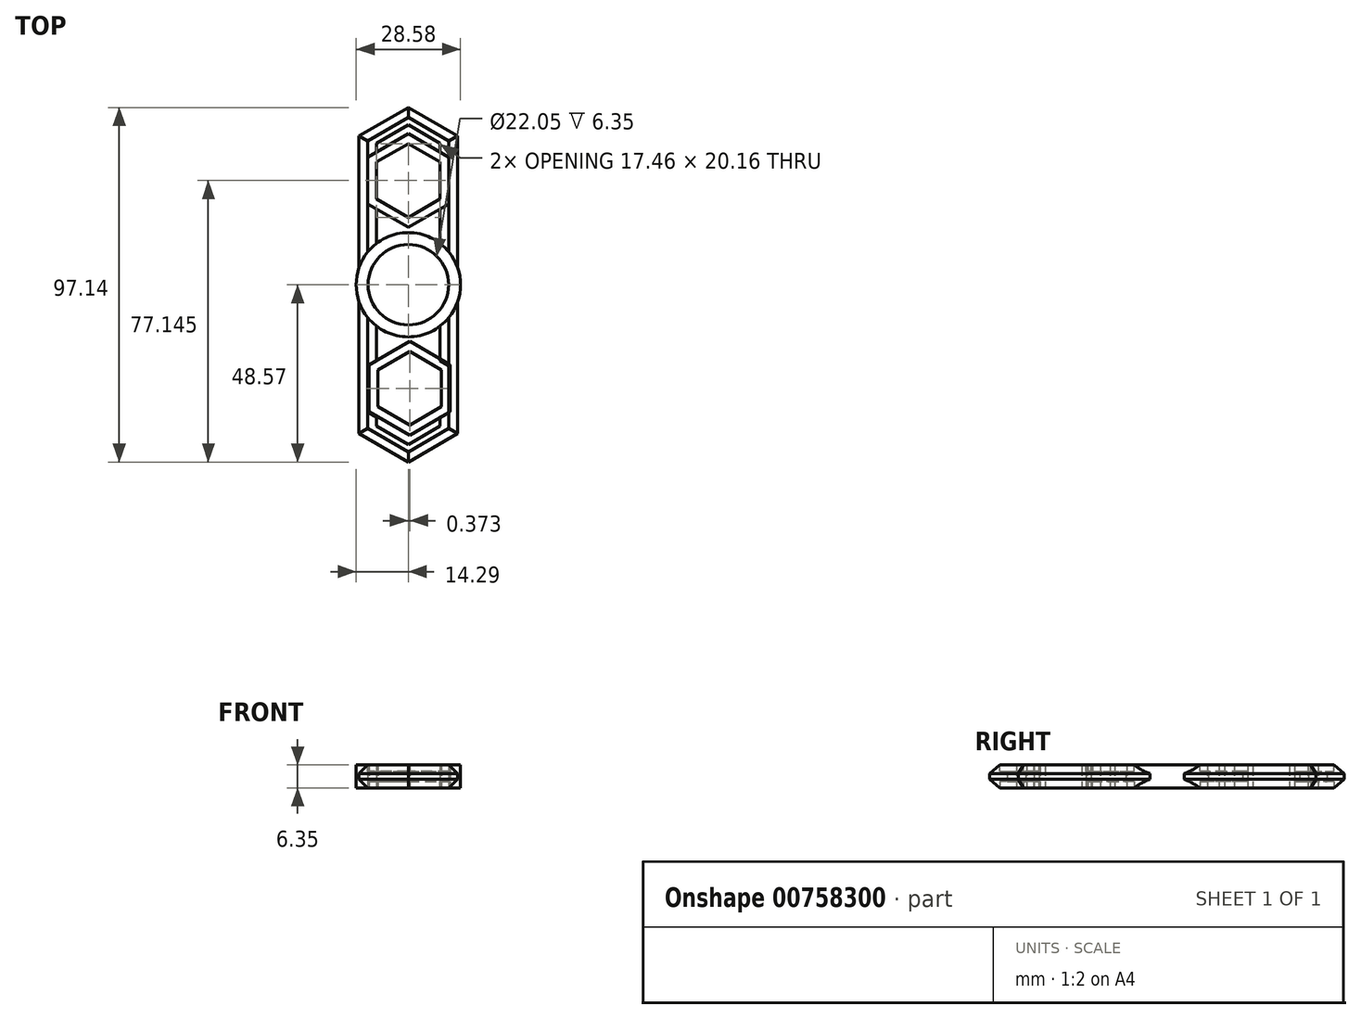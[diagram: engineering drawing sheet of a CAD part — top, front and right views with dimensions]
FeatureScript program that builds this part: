
annotation { "Feature Type Name" : "Feature", "Feature Type Description" : "" }
export const myFeature = defineFeature(function(context is Context, id is Id, definition is map)
    precondition{}
    {
        {
            var Q0;
            Q0=qCreatedBy(makeId("Top.planeOp"),FACE);
            var sketch = newSketch(context, id + "F0", { "sketchPlane" : qUnion([Q0])});
            skCircle(sketch, "E0", {"center": v(0, 0) * mm, "radius": 11.02 * mm});
            skCircle(sketch, "E1", {"center": v(0, 0) * mm, "radius": 14.29 * mm});
            skCircle(sketch, "E2.cCircle", {"center": v(0, 28.58) * mm, "radius": 8.73 * mm, "construction": true});
            skLineSegment(sketch, "E2.0", {"start": v(8.73, 33.62) * mm, "end": v(8.73, 23.53) * mm});
            skLineSegment(sketch, "E2.1", {"start": v(8.73, 23.53) * mm, "end": v(0, 18.5) * mm});
            skLineSegment(sketch, "E2.2", {"start": v(0, 18.5) * mm, "end": v(-8.73, 23.53) * mm});
            skLineSegment(sketch, "E2.3", {"start": v(-8.73, 23.53) * mm, "end": v(-8.73, 33.62) * mm});
            skLineSegment(sketch, "E2.4", {"start": v(-8.73, 33.62) * mm, "end": v(0, 38.66) * mm});
            skLineSegment(sketch, "E2.5", {"start": v(0, 38.66) * mm, "end": v(8.73, 33.62) * mm});
            skPoint(sketch, "E2.0.midPoint", {"position": v(8.73, 28.58) * mm});
            skCircle(sketch, "E3.cCircle", {"center": v(0, 28.58) * mm, "radius": 11.11 * mm, "construction": true});
            skLineSegment(sketch, "E3.0", {"start": v(11.11, 35) * mm, "end": v(11.11, 22.16) * mm});
            skLineSegment(sketch, "E3.1", {"start": v(11.11, 22.16) * mm, "end": v(0, 15.74) * mm});
            skLineSegment(sketch, "E3.2", {"start": v(0, 15.74) * mm, "end": v(-11.11, 22.16) * mm});
            skLineSegment(sketch, "E3.3", {"start": v(-11.11, 22.16) * mm, "end": v(-11.11, 35) * mm});
            skLineSegment(sketch, "E3.4", {"start": v(-11.11, 35) * mm, "end": v(0, 41.4) * mm});
            skLineSegment(sketch, "E3.5", {"start": v(0, 41.4) * mm, "end": v(11.11, 35) * mm});
            skPoint(sketch, "E3.0.midPoint", {"position": v(11.11, 28.58) * mm});
            skLineSegment(sketch, "E4.1.0", {"start": v(0.37, -38.45) * mm, "end": v(-8.36, -33.41) * mm});
            skLineSegment(sketch, "E4.1.1", {"start": v(9.1, -23.33) * mm, "end": v(9.1, -33.41) * mm});
            skCircle(sketch, "E4.1.2", {"center": v(0.37, -28.37) * mm, "radius": 8.73 * mm, "construction": true});
            skPoint(sketch, "E4.1.3", {"position": v(-10.74, -28.37) * mm});
            skLineSegment(sketch, "E4.1.4", {"start": v(0.37, -41.2) * mm, "end": v(-10.74, -34.79) * mm});
            skLineSegment(sketch, "E4.1.5", {"start": v(11.49, -34.79) * mm, "end": v(0.37, -41.2) * mm});
            skLineSegment(sketch, "E4.1.6", {"start": v(11.49, -21.96) * mm, "end": v(11.49, -34.79) * mm});
            skPoint(sketch, "E4.1.7", {"position": v(-8.36, -28.37) * mm});
            skLineSegment(sketch, "E4.1.8", {"start": v(0.37, -15.54) * mm, "end": v(11.49, -21.96) * mm});
            skLineSegment(sketch, "E4.1.9", {"start": v(-10.74, -21.96) * mm, "end": v(0.37, -15.54) * mm});
            skCircle(sketch, "E4.1.10", {"center": v(0.37, -28.37) * mm, "radius": 11.11 * mm, "construction": true});
            skLineSegment(sketch, "E4.1.11", {"start": v(9.1, -33.41) * mm, "end": v(0.37, -38.45) * mm});
            skLineSegment(sketch, "E4.1.12", {"start": v(0.37, -18.29) * mm, "end": v(9.1, -23.33) * mm});
            skLineSegment(sketch, "E4.1.13", {"start": v(-8.36, -23.33) * mm, "end": v(0.37, -18.29) * mm});
            skLineSegment(sketch, "E4.1.14", {"start": v(-8.36, -33.41) * mm, "end": v(-8.36, -23.33) * mm});
            skLineSegment(sketch, "E4.1.15", {"start": v(-10.74, -34.79) * mm, "end": v(-10.74, -21.96) * mm});
            skPoint(sketch, "E4.center", {"position": v(0.19, 0.1) * mm});
            skSolve(sketch);
        }
        {
            var Q0;
            Q0=makeQuery(id+"F0.imprint","IMPRINT",FACE,{"disambiguationData":[TD([[makeQuery(id+"F0.imprint","IMPRINT",EDGE,{"derivedFrom":sQuery(id+"F0.wireOp",EDGE,"E0")}),1.0]])]});
            var sketch = newSketch(context, id + "F1", { "sketchPlane" : qUnion([Q0])});
            skLineSegment(sketch, "E5.3", {"start": v(0, 41.4) * mm, "end": v(11.11, 35) * mm});
            skCircle(sketch, "E5.4", {"center": v(0, 28.58) * mm, "radius": 8.73 * mm});
            skLineSegment(sketch, "E5.5", {"start": v(8.73, 23.53) * mm, "end": v(0, 18.5) * mm});
            skLineSegment(sketch, "E5.6", {"start": v(0, 18.5) * mm, "end": v(-8.73, 23.53) * mm});
            skLineSegment(sketch, "E5.7", {"start": v(-8.73, 23.53) * mm, "end": v(-8.73, 33.62) * mm});
            skLineSegment(sketch, "E5.8", {"start": v(-8.73, 33.62) * mm, "end": v(0, 38.66) * mm});
            skLineSegment(sketch, "E5.9", {"start": v(0, 38.66) * mm, "end": v(8.73, 33.62) * mm});
            skLineSegment(sketch, "E5.10", {"start": v(11.11, 35) * mm, "end": v(11.11, 22.16) * mm});
            skLineSegment(sketch, "E5.11", {"start": v(11.11, 22.16) * mm, "end": v(0, 15.74) * mm});
            skLineSegment(sketch, "E5.18", {"start": v(8.73, 33.62) * mm, "end": v(8.73, 23.53) * mm});
            skLineSegment(sketch, "E6.2", {"start": v(-11.11, 22.16) * mm, "end": v(-11.11, 35) * mm});
            skLineSegment(sketch, "E6.3", {"start": v(-11.11, 35) * mm, "end": v(0, 41.4) * mm});
            skCircle(sketch, "E6.4", {"center": v(0, 0) * mm, "radius": 11.02 * mm});
            skCircle(sketch, "E6.5", {"center": v(0, 0) * mm, "radius": 14.29 * mm});
            skCircle(sketch, "E6.6", {"center": v(0, 28.58) * mm, "radius": 11.11 * mm});
            skLineSegment(sketch, "E6.7", {"start": v(0, 15.74) * mm, "end": v(-11.11, 22.16) * mm});
            skLineSegment(sketch, "E7", {"start": v(-11.11, 22.16) * mm, "end": v(-11.11, 8.98) * mm});
            skLineSegment(sketch, "E8", {"start": v(11.11, 22.16) * mm, "end": v(11.11, 8.98) * mm});
            skLineSegment(sketch, "E9", {"start": v(-11.11, 37.38) * mm, "end": v(0, 43.8) * mm});
            skLineSegment(sketch, "E10", {"start": v(0, 43.8) * mm, "end": v(11.11, 37.38) * mm});
            skLineSegment(sketch, "E11", {"start": v(11.11, 37.38) * mm, "end": v(11.11, 35) * mm});
            skLineSegment(sketch, "E12", {"start": v(-11.11, 35) * mm, "end": v(-11.11, 37.38) * mm});
            skLineSegment(sketch, "E13", {"start": v(-8.73, 20.78) * mm, "end": v(-8.73, 11.3) * mm});
            skLineSegment(sketch, "E14", {"start": v(8.73, 20.78) * mm, "end": v(8.73, 11.3) * mm});
            skLineSegment(sketch, "E15", {"start": v(-13.5, 0) * mm, "end": v(-13.5, 38.39) * mm});
            skLineSegment(sketch, "E16", {"start": v(-13.5, 38.39) * mm, "end": v(0, 46.18) * mm});
            skLineSegment(sketch, "E17", {"start": v(0, 46.18) * mm, "end": v(13.5, 38.39) * mm});
            skLineSegment(sketch, "E18", {"start": v(13.5, 38.39) * mm, "end": v(13.5, 0) * mm});
            skLineSegment(sketch, "E19", {"start": v(-8.73, 36.37) * mm, "end": v(-8.73, 38.75) * mm});
            skLineSegment(sketch, "E20", {"start": v(8.73, 36.37) * mm, "end": v(8.73, 38.75) * mm});
            skLineSegment(sketch, "E21.MirrorCS", {"start": v(11.11, -37.38) * mm, "end": v(11.11, -35) * mm});
            skLineSegment(sketch, "E22.MirrorCS", {"start": v(-11.11, -35) * mm, "end": v(-11.11, -37.38) * mm});
            skLineSegment(sketch, "E23.MirrorCS", {"start": v(-8.73, -36.37) * mm, "end": v(-8.73, -38.75) * mm});
            skLineSegment(sketch, "E24.MirrorCS", {"start": v(-8.73, -23.53) * mm, "end": v(-8.73, -33.62) * mm});
            skLineSegment(sketch, "E25.MirrorCS", {"start": v(8.73, -36.37) * mm, "end": v(8.73, -38.75) * mm});
            skLineSegment(sketch, "E26.MirrorCS", {"start": v(11.11, -22.16) * mm, "end": v(0, -15.74) * mm});
            skCircle(sketch, "E27.MirrorC", {"center": v(0, -28.58) * mm, "radius": 8.73 * mm});
            skLineSegment(sketch, "E28.MirrorCS", {"start": v(8.73, -23.53) * mm, "end": v(0, -18.5) * mm});
            skLineSegment(sketch, "E29.MirrorCS", {"start": v(0, -18.5) * mm, "end": v(-8.73, -23.53) * mm});
            skLineSegment(sketch, "E30.MirrorCS", {"start": v(8.73, -33.62) * mm, "end": v(8.73, -23.53) * mm});
            skLineSegment(sketch, "E31.MirrorCS", {"start": v(0, -41.4) * mm, "end": v(11.11, -35) * mm});
            skLineSegment(sketch, "E32.MirrorCS", {"start": v(-8.73, -33.62) * mm, "end": v(0, -38.66) * mm});
            skLineSegment(sketch, "E33.MirrorCS", {"start": v(11.11, -35) * mm, "end": v(11.11, -22.16) * mm});
            skLineSegment(sketch, "E34.MirrorCS", {"start": v(0, -38.66) * mm, "end": v(8.73, -33.62) * mm});
            skLineSegment(sketch, "E35.MirrorCS", {"start": v(-13.5, -38.39) * mm, "end": v(0, -46.18) * mm});
            skLineSegment(sketch, "E36.MirrorCS", {"start": v(8.73, -20.78) * mm, "end": v(8.73, -11.3) * mm});
            skLineSegment(sketch, "E37.MirrorCS", {"start": v(-11.11, -35) * mm, "end": v(0, -41.4) * mm});
            skLineSegment(sketch, "E38.MirrorCS", {"start": v(0, -15.74) * mm, "end": v(-11.11, -22.16) * mm});
            skLineSegment(sketch, "E39.MirrorCS", {"start": v(-11.11, -37.38) * mm, "end": v(0, -43.8) * mm});
            skLineSegment(sketch, "E40.MirrorCS", {"start": v(11.11, -22.16) * mm, "end": v(11.11, -8.98) * mm});
            skLineSegment(sketch, "E41.MirrorCS", {"start": v(0, -46.18) * mm, "end": v(13.5, -38.39) * mm});
            skLineSegment(sketch, "E42.MirrorCS", {"start": v(-8.73, -20.78) * mm, "end": v(-8.73, -11.3) * mm});
            skLineSegment(sketch, "E43.MirrorCS", {"start": v(-11.11, -22.16) * mm, "end": v(-11.11, -35) * mm});
            skCircle(sketch, "E44.MirrorC", {"center": v(0, -28.58) * mm, "radius": 11.11 * mm});
            skLineSegment(sketch, "E45.MirrorCS", {"start": v(-11.11, -22.16) * mm, "end": v(-11.11, -8.98) * mm});
            skLineSegment(sketch, "E46.MirrorCS", {"start": v(0, -43.8) * mm, "end": v(11.11, -37.38) * mm});
            skLineSegment(sketch, "E47.MirrorCS", {"start": v(13.5, -38.39) * mm, "end": v(13.5, 0) * mm});
            skLineSegment(sketch, "E48.MirrorCS", {"start": v(-13.5, 0) * mm, "end": v(-13.5, -38.39) * mm});
            skLineSegment(sketch, "E49", {"start": v(-13.5, 38.39) * mm, "end": v(-13.5, 40.78) * mm});
            skLineSegment(sketch, "E50", {"start": v(-13.5, 40.78) * mm, "end": v(0, 48.57) * mm});
            skLineSegment(sketch, "E51", {"start": v(0, 48.57) * mm, "end": v(13.5, 40.78) * mm});
            skLineSegment(sketch, "E52", {"start": v(13.5, 40.78) * mm, "end": v(13.5, 38.39) * mm});
            skLineSegment(sketch, "E53.MirrorCS", {"start": v(0, -48.57) * mm, "end": v(13.5, -40.78) * mm});
            skLineSegment(sketch, "E54.MirrorCS", {"start": v(-13.5, -40.78) * mm, "end": v(0, -48.57) * mm});
            skLineSegment(sketch, "E55.MirrorCS", {"start": v(-13.5, -38.39) * mm, "end": v(-13.5, -40.78) * mm});
            skLineSegment(sketch, "E56.MirrorCS", {"start": v(13.5, -40.78) * mm, "end": v(13.5, -38.39) * mm});
            skSolve(sketch);
        }
        {
            var Q0;
            Q0 = qSketchRegion(id + "F1", true);
            var Q1;
            Q1=makeQuery(id+"F0.imprint","IMPRINT",FACE,{"disambiguationData":[TD([[makeQuery(id+"F0.imprint","IMPRINT",EDGE,{"derivedFrom":sQuery(id+"F0.wireOp",EDGE,"E2.0")}),1.0]])]});
            var Q2;
            Q2=makeQuery(id+"F0.imprint","IMPRINT",FACE,{"disambiguationData":[TD([[makeQuery(id+"F0.imprint","IMPRINT",EDGE,{"derivedFrom":sQuery(id+"F0.wireOp",EDGE,"E4.1.0")}),1.0]])]});
            var Q3;
            {var subQ0=sQuery(id+"F1.wireOp",EDGE,"E7");Q3=makeQuery(id+"F1.imprint","IMPRINT",FACE,{"disambiguationData":[TD([[makeQuery(id+"F1.imprint","IMPRINT",EDGE,{"derivedFrom":subQ0}),1.0]])]});}
            var Q4;
            {var subQ0=sQuery(id+"F1.wireOp",EDGE,"E8");Q4=makeQuery(id+"F1.imprint","IMPRINT",FACE,{"disambiguationData":[TD([[makeQuery(id+"F1.imprint","IMPRINT",EDGE,{"derivedFrom":subQ0}),-1.0]])]});}
            var Q5;
            {var subQ0=sQuery(id+"F1.wireOp",EDGE,"E11");Q5=makeQuery(id+"F1.imprint","IMPRINT",FACE,{"disambiguationData":[TD([[makeQuery(id+"F1.imprint","IMPRINT",EDGE,{"derivedFrom":subQ0}),-1.0]])]});}
            var Q6;
            {var subQ0=sQuery(id+"F1.wireOp",EDGE,"E12");Q6=makeQuery(id+"F1.imprint","IMPRINT",FACE,{"disambiguationData":[TD([[makeQuery(id+"F1.imprint","IMPRINT",EDGE,{"derivedFrom":subQ0}),-1.0]])]});}
            var Q7;
            {var subQ0=sQuery(id+"F1.wireOp",EDGE,"E42.MirrorCS");Q7=makeQuery(id+"F1.imprint","IMPRINT",FACE,{"disambiguationData":[TD([[makeQuery(id+"F1.imprint","IMPRINT",EDGE,{"derivedFrom":subQ0}),1.0]])]});}
            var Q8;
            {var subQ0=sQuery(id+"F1.wireOp",EDGE,"E36.MirrorCS");Q8=makeQuery(id+"F1.imprint","IMPRINT",FACE,{"disambiguationData":[TD([[makeQuery(id+"F1.imprint","IMPRINT",EDGE,{"derivedFrom":subQ0}),-1.0]])]});}
            var Q9;
            {var subQ0=sQuery(id+"F1.wireOp",EDGE,"E21.MirrorCS");Q9=makeQuery(id+"F1.imprint","IMPRINT",FACE,{"disambiguationData":[TD([[makeQuery(id+"F1.imprint","IMPRINT",EDGE,{"derivedFrom":subQ0}),1.0]])]});}
            var Q10;
            {var subQ0=sQuery(id+"F1.wireOp",EDGE,"E22.MirrorCS");Q10=makeQuery(id+"F1.imprint","IMPRINT",FACE,{"disambiguationData":[TD([[makeQuery(id+"F1.imprint","IMPRINT",EDGE,{"derivedFrom":subQ0}),1.0]])]});}
            var Q11;
            {var subQ0=sQuery(id+"F1.wireOp",EDGE,"E22.MirrorCS");Q11=makeQuery(id+"F1.imprint","IMPRINT",FACE,{"disambiguationData":[TD([[makeQuery(id+"F1.imprint","IMPRINT",EDGE,{"derivedFrom":subQ0}),1.0]])]});}
            var Q12;
            {var subQ0=sQuery(id+"F1.wireOp",EDGE,"E21.MirrorCS");Q12=makeQuery(id+"F1.imprint","IMPRINT",FACE,{"disambiguationData":[TD([[makeQuery(id+"F1.imprint","IMPRINT",EDGE,{"derivedFrom":subQ0}),1.0]])]});}
            extrude(context, id + "F2", {"entities" : qUnion([Q0, Q1, Q2, Q3, Q4, Q5, Q6, Q7, Q8, Q9, Q10, Q11, Q12]), "depth" : 6.35 * mm, "offsetDistance" : 25.4 * mm});
        }
        {
            var Q0;
            Q0=makeQuery(id+"F2.opExtrude","CAP_EDGE",EDGE,{"disambiguationData":[OSD([sQuery(id+"F1.wireOp",EDGE,"E47.MirrorCS"),sQuery(id+"F1.wireOp",EDGE,"E56.MirrorCS")])],"isStart":false});
            var Q1;
            Q1=makeQuery(id+"F2.opExtrude","CAP_EDGE",EDGE,{"disambiguationData":[OSD([sQuery(id+"F1.wireOp",EDGE,"E18"),sQuery(id+"F1.wireOp",EDGE,"E52")])],"isStart":false});
            var Q2;
            Q2=makeQuery(id+"F2.opExtrude","CAP_EDGE",EDGE,{"disambiguationData":[OSD([sQuery(id+"F1.wireOp",EDGE,"E18"),sQuery(id+"F1.wireOp",EDGE,"E52")])],"isStart":true});
            var Q3;
            Q3=makeQuery(id+"F2.opExtrude","CAP_EDGE",EDGE,{"disambiguationData":[OSD([sQuery(id+"F1.wireOp",EDGE,"E47.MirrorCS"),sQuery(id+"F1.wireOp",EDGE,"E56.MirrorCS")])],"isStart":true});
            var Q4;
            Q4=makeQuery(id+"F2.opExtrude","CAP_EDGE",EDGE,{"disambiguationData":[OSD([sQuery(id+"F1.wireOp",EDGE,"E48.MirrorCS"),sQuery(id+"F1.wireOp",EDGE,"E55.MirrorCS")])],"isStart":true});
            var Q5;
            Q5=makeQuery(id+"F2.opExtrude","CAP_EDGE",EDGE,{"disambiguationData":[OSD([sQuery(id+"F1.wireOp",EDGE,"E15"),sQuery(id+"F1.wireOp",EDGE,"E49")])],"isStart":true});
            var Q6;
            Q6=makeQuery(id+"F2.opExtrude","CAP_EDGE",EDGE,{"disambiguationData":[OSD([sQuery(id+"F1.wireOp",EDGE,"E50")])],"isStart":true});
            var Q7;
            Q7=makeQuery(id+"F2.opExtrude","CAP_EDGE",EDGE,{"disambiguationData":[OSD([sQuery(id+"F1.wireOp",EDGE,"E51")])],"isStart":true});
            var Q8;
            Q8=makeQuery(id+"F2.opExtrude","CAP_EDGE",EDGE,{"disambiguationData":[OSD([sQuery(id+"F1.wireOp",EDGE,"E51")])],"isStart":false});
            var Q9;
            Q9=makeQuery(id+"F2.opExtrude","CAP_EDGE",EDGE,{"disambiguationData":[OSD([sQuery(id+"F1.wireOp",EDGE,"E50")])],"isStart":false});
            var Q10;
            Q10=makeQuery(id+"F2.opExtrude","CAP_EDGE",EDGE,{"disambiguationData":[OSD([sQuery(id+"F1.wireOp",EDGE,"E54.MirrorCS")])],"isStart":false});
            var Q11;
            Q11=makeQuery(id+"F2.opExtrude","CAP_EDGE",EDGE,{"disambiguationData":[OSD([sQuery(id+"F1.wireOp",EDGE,"E48.MirrorCS"),sQuery(id+"F1.wireOp",EDGE,"E55.MirrorCS")])],"isStart":false});
            var Q12;
            Q12=makeQuery(id+"F2.opExtrude","CAP_EDGE",EDGE,{"disambiguationData":[OSD([sQuery(id+"F1.wireOp",EDGE,"E53.MirrorCS")])],"isStart":false});
            var Q13;
            Q13=makeQuery(id+"F2.opExtrude","CAP_EDGE",EDGE,{"disambiguationData":[OSD([sQuery(id+"F1.wireOp",EDGE,"E53.MirrorCS")])],"isStart":true});
            var Q14;
            Q14=makeQuery(id+"F2.opExtrude","CAP_EDGE",EDGE,{"disambiguationData":[OSD([sQuery(id+"F1.wireOp",EDGE,"E54.MirrorCS")])],"isStart":true});
            var Q15;
            Q15=makeQuery(id+"F2.opExtrude","CAP_EDGE",EDGE,{"disambiguationData":[OSD([sQuery(id+"F1.wireOp",EDGE,"E15"),sQuery(id+"F1.wireOp",EDGE,"E49")])],"isStart":false});
            chamfer(context, id + "F3", {"entities" : qUnion([Q0, Q1, Q2, Q3, Q4, Q5, Q6, Q7, Q8, Q9, Q10, Q11, Q12, Q13, Q14, Q15]), "width" : 2.4 * mm, "tangentPropagation" : true});
        }
        {
            var Q0;
            Q0=makeQuery(id+"F3.opChamfer","SPLIT",FACE,{"disambiguationData":[OD(2.0)],"derivedFrom":makeQuery(id+"F2.opExtrude","CAP_FACE",FACE,{"disambiguationData":[OSD([sQuery(id+"F1.wireOp",EDGE,"E6.2"),sQuery(id+"F1.wireOp",EDGE,"E6.3"),sQuery(id+"F1.wireOp",EDGE,"E6.4"),sQuery(id+"F1.wireOp",EDGE,"E6.5"),sQuery(id+"F1.wireOp",EDGE,"E6.7"),sQuery(id+"F1.wireOp",EDGE,"E5.3"),sQuery(id+"F1.wireOp",EDGE,"E5.10"),sQuery(id+"F1.wireOp",EDGE,"E5.11"),sQuery(id+"F1.wireOp",EDGE,"E9"),sQuery(id+"F1.wireOp",EDGE,"E10"),sQuery(id+"F1.wireOp",EDGE,"E13"),sQuery(id+"F1.wireOp",EDGE,"E14"),sQuery(id+"F1.wireOp",EDGE,"E15"),sQuery(id+"F1.wireOp",EDGE,"E18"),sQuery(id+"F1.wireOp",EDGE,"E19"),sQuery(id+"F1.wireOp",EDGE,"E20"),sQuery(id+"F1.wireOp",EDGE,"E26.MirrorCS"),sQuery(id+"F1.wireOp",EDGE,"E36.MirrorCS"),sQuery(id+"F1.wireOp",EDGE,"E38.MirrorCS"),sQuery(id+"F1.wireOp",EDGE,"E42.MirrorCS"),sQuery(id+"F1.wireOp",EDGE,"E43.MirrorCS"),sQuery(id+"F1.wireOp",EDGE,"E33.MirrorCS"),sQuery(id+"F1.wireOp",EDGE,"E47.MirrorCS"),sQuery(id+"F1.wireOp",EDGE,"E48.MirrorCS"),sQuery(id+"F1.wireOp",EDGE,"E49"),sQuery(id+"F1.wireOp",EDGE,"E50"),sQuery(id+"F1.wireOp",EDGE,"E51"),sQuery(id+"F1.wireOp",EDGE,"E52"),sQuery(id+"F1.wireOp",EDGE,"E53.MirrorCS"),sQuery(id+"F1.wireOp",EDGE,"E54.MirrorCS"),sQuery(id+"F1.wireOp",EDGE,"E55.MirrorCS"),sQuery(id+"F1.wireOp",EDGE,"E56.MirrorCS"),sQuery(id+"F1.wireOp",EDGE,"E23.MirrorCS"),sQuery(id+"F1.wireOp",EDGE,"E25.MirrorCS"),sQuery(id+"F1.wireOp",EDGE,"E39.MirrorCS"),sQuery(id+"F1.wireOp",EDGE,"E46.MirrorCS"),sQuery(id+"F1.wireOp",EDGE,"E37.MirrorCS"),sQuery(id+"F1.wireOp",EDGE,"E31.MirrorCS")])],"isStart":false})});
            var sketch = newSketch(context, id + "F4", { "sketchPlane" : qUnion([Q0])});
            skCircle(sketch, "E57", {"center": v(0, 0) * mm, "radius": 14.29 * mm});
            skSolve(sketch);
        }
        {
            var Q0;
            {var subQ5=sQuery(id+"F1.wireOp",EDGE,"E26.MirrorCS");Q0=makeQuery(id+"F4.imprint","IMPRINT",FACE,{"disambiguationData":[TD([[makeQuery(id+"F4.imprint","IMPRINT",EDGE,{"derivedFrom":makeQuery(id+"F2.opExtrude","CAP_EDGE",EDGE,{"disambiguationData":[OSD([subQ5])],"isStart":false})}),-1.0]])]});}
            var Q1;
            Q1=makeQuery(id+"F3.opChamfer","SPLIT",FACE,{"disambiguationData":[OD(1.0)],"derivedFrom":makeQuery(id+"F2.opExtrude","CAP_FACE",FACE,{"disambiguationData":[OSD([sQuery(id+"F1.wireOp",EDGE,"E6.2"),sQuery(id+"F1.wireOp",EDGE,"E6.3"),sQuery(id+"F1.wireOp",EDGE,"E6.4"),sQuery(id+"F1.wireOp",EDGE,"E6.5"),sQuery(id+"F1.wireOp",EDGE,"E6.7"),sQuery(id+"F1.wireOp",EDGE,"E5.3"),sQuery(id+"F1.wireOp",EDGE,"E5.10"),sQuery(id+"F1.wireOp",EDGE,"E5.11"),sQuery(id+"F1.wireOp",EDGE,"E9"),sQuery(id+"F1.wireOp",EDGE,"E10"),sQuery(id+"F1.wireOp",EDGE,"E13"),sQuery(id+"F1.wireOp",EDGE,"E14"),sQuery(id+"F1.wireOp",EDGE,"E15"),sQuery(id+"F1.wireOp",EDGE,"E18"),sQuery(id+"F1.wireOp",EDGE,"E19"),sQuery(id+"F1.wireOp",EDGE,"E20"),sQuery(id+"F1.wireOp",EDGE,"E26.MirrorCS"),sQuery(id+"F1.wireOp",EDGE,"E36.MirrorCS"),sQuery(id+"F1.wireOp",EDGE,"E38.MirrorCS"),sQuery(id+"F1.wireOp",EDGE,"E42.MirrorCS"),sQuery(id+"F1.wireOp",EDGE,"E43.MirrorCS"),sQuery(id+"F1.wireOp",EDGE,"E33.MirrorCS"),sQuery(id+"F1.wireOp",EDGE,"E47.MirrorCS"),sQuery(id+"F1.wireOp",EDGE,"E48.MirrorCS"),sQuery(id+"F1.wireOp",EDGE,"E49"),sQuery(id+"F1.wireOp",EDGE,"E50"),sQuery(id+"F1.wireOp",EDGE,"E51"),sQuery(id+"F1.wireOp",EDGE,"E52"),sQuery(id+"F1.wireOp",EDGE,"E53.MirrorCS"),sQuery(id+"F1.wireOp",EDGE,"E54.MirrorCS"),sQuery(id+"F1.wireOp",EDGE,"E55.MirrorCS"),sQuery(id+"F1.wireOp",EDGE,"E56.MirrorCS"),sQuery(id+"F1.wireOp",EDGE,"E23.MirrorCS"),sQuery(id+"F1.wireOp",EDGE,"E25.MirrorCS"),sQuery(id+"F1.wireOp",EDGE,"E39.MirrorCS"),sQuery(id+"F1.wireOp",EDGE,"E46.MirrorCS"),sQuery(id+"F1.wireOp",EDGE,"E37.MirrorCS"),sQuery(id+"F1.wireOp",EDGE,"E31.MirrorCS")])],"isStart":false})});
            var Q2;
            {var subQ5=sQuery(id+"F1.wireOp",EDGE,"E38.MirrorCS");Q2=makeQuery(id+"F4.imprint","IMPRINT",FACE,{"disambiguationData":[TD([[makeQuery(id+"F4.imprint","IMPRINT",EDGE,{"derivedFrom":makeQuery(id+"F2.opExtrude","CAP_EDGE",EDGE,{"disambiguationData":[OSD([subQ5])],"isStart":false})}),-1.0]])]});}
            var Q3;
            {var subQ5=sQuery(id+"F1.wireOp",EDGE,"E5.11");Q3=makeQuery(id+"F4.imprint","IMPRINT",FACE,{"disambiguationData":[TD([[makeQuery(id+"F4.imprint","IMPRINT",EDGE,{"derivedFrom":makeQuery(id+"F2.opExtrude","CAP_EDGE",EDGE,{"disambiguationData":[OSD([subQ5])],"isStart":false})}),1.0]])]});}
            var Q4;
            {var subQ5=sQuery(id+"F1.wireOp",EDGE,"E6.7");Q4=makeQuery(id+"F4.imprint","IMPRINT",FACE,{"disambiguationData":[TD([[makeQuery(id+"F4.imprint","IMPRINT",EDGE,{"derivedFrom":makeQuery(id+"F2.opExtrude","CAP_EDGE",EDGE,{"disambiguationData":[OSD([subQ5])],"isStart":false})}),1.0]])]});}
            var Q5;
            Q5=makeQuery(id+"F3.opChamfer","SPLIT",FACE,{"disambiguationData":[OD(0.0)],"derivedFrom":makeQuery(id+"F2.opExtrude","CAP_FACE",FACE,{"disambiguationData":[OSD([sQuery(id+"F1.wireOp",EDGE,"E6.2"),sQuery(id+"F1.wireOp",EDGE,"E6.3"),sQuery(id+"F1.wireOp",EDGE,"E6.4"),sQuery(id+"F1.wireOp",EDGE,"E6.5"),sQuery(id+"F1.wireOp",EDGE,"E6.7"),sQuery(id+"F1.wireOp",EDGE,"E5.3"),sQuery(id+"F1.wireOp",EDGE,"E5.10"),sQuery(id+"F1.wireOp",EDGE,"E5.11"),sQuery(id+"F1.wireOp",EDGE,"E9"),sQuery(id+"F1.wireOp",EDGE,"E10"),sQuery(id+"F1.wireOp",EDGE,"E13"),sQuery(id+"F1.wireOp",EDGE,"E14"),sQuery(id+"F1.wireOp",EDGE,"E15"),sQuery(id+"F1.wireOp",EDGE,"E18"),sQuery(id+"F1.wireOp",EDGE,"E19"),sQuery(id+"F1.wireOp",EDGE,"E20"),sQuery(id+"F1.wireOp",EDGE,"E26.MirrorCS"),sQuery(id+"F1.wireOp",EDGE,"E36.MirrorCS"),sQuery(id+"F1.wireOp",EDGE,"E38.MirrorCS"),sQuery(id+"F1.wireOp",EDGE,"E42.MirrorCS"),sQuery(id+"F1.wireOp",EDGE,"E43.MirrorCS"),sQuery(id+"F1.wireOp",EDGE,"E33.MirrorCS"),sQuery(id+"F1.wireOp",EDGE,"E47.MirrorCS"),sQuery(id+"F1.wireOp",EDGE,"E48.MirrorCS"),sQuery(id+"F1.wireOp",EDGE,"E49"),sQuery(id+"F1.wireOp",EDGE,"E50"),sQuery(id+"F1.wireOp",EDGE,"E51"),sQuery(id+"F1.wireOp",EDGE,"E52"),sQuery(id+"F1.wireOp",EDGE,"E53.MirrorCS"),sQuery(id+"F1.wireOp",EDGE,"E54.MirrorCS"),sQuery(id+"F1.wireOp",EDGE,"E55.MirrorCS"),sQuery(id+"F1.wireOp",EDGE,"E56.MirrorCS"),sQuery(id+"F1.wireOp",EDGE,"E23.MirrorCS"),sQuery(id+"F1.wireOp",EDGE,"E25.MirrorCS"),sQuery(id+"F1.wireOp",EDGE,"E39.MirrorCS"),sQuery(id+"F1.wireOp",EDGE,"E46.MirrorCS"),sQuery(id+"F1.wireOp",EDGE,"E37.MirrorCS"),sQuery(id+"F1.wireOp",EDGE,"E31.MirrorCS")])],"isStart":false})});
            extrude(context, id + "F5", {"entities" : qUnion([Q0, Q1, Q2, Q3, Q4, Q5]), "operationType" : NewBodyOperationType.REMOVE, "oppositeDirection" : true, "depth" : 1.78 * mm, "offsetDistance" : 25.4 * mm});
        }
        {
            var Q0;
            Q0=makeQuery(id+"F3.opChamfer","SPLIT",FACE,{"disambiguationData":[OD(2.0)],"derivedFrom":makeQuery(id+"F2.opExtrude","CAP_FACE",FACE,{"disambiguationData":[OSD([sQuery(id+"F1.wireOp",EDGE,"E6.2"),sQuery(id+"F1.wireOp",EDGE,"E6.3"),sQuery(id+"F1.wireOp",EDGE,"E6.4"),sQuery(id+"F1.wireOp",EDGE,"E6.5"),sQuery(id+"F1.wireOp",EDGE,"E6.7"),sQuery(id+"F1.wireOp",EDGE,"E5.3"),sQuery(id+"F1.wireOp",EDGE,"E5.10"),sQuery(id+"F1.wireOp",EDGE,"E5.11"),sQuery(id+"F1.wireOp",EDGE,"E9"),sQuery(id+"F1.wireOp",EDGE,"E10"),sQuery(id+"F1.wireOp",EDGE,"E13"),sQuery(id+"F1.wireOp",EDGE,"E14"),sQuery(id+"F1.wireOp",EDGE,"E15"),sQuery(id+"F1.wireOp",EDGE,"E18"),sQuery(id+"F1.wireOp",EDGE,"E19"),sQuery(id+"F1.wireOp",EDGE,"E20"),sQuery(id+"F1.wireOp",EDGE,"E26.MirrorCS"),sQuery(id+"F1.wireOp",EDGE,"E36.MirrorCS"),sQuery(id+"F1.wireOp",EDGE,"E38.MirrorCS"),sQuery(id+"F1.wireOp",EDGE,"E42.MirrorCS"),sQuery(id+"F1.wireOp",EDGE,"E43.MirrorCS"),sQuery(id+"F1.wireOp",EDGE,"E33.MirrorCS"),sQuery(id+"F1.wireOp",EDGE,"E47.MirrorCS"),sQuery(id+"F1.wireOp",EDGE,"E48.MirrorCS"),sQuery(id+"F1.wireOp",EDGE,"E49"),sQuery(id+"F1.wireOp",EDGE,"E50"),sQuery(id+"F1.wireOp",EDGE,"E51"),sQuery(id+"F1.wireOp",EDGE,"E52"),sQuery(id+"F1.wireOp",EDGE,"E53.MirrorCS"),sQuery(id+"F1.wireOp",EDGE,"E54.MirrorCS"),sQuery(id+"F1.wireOp",EDGE,"E55.MirrorCS"),sQuery(id+"F1.wireOp",EDGE,"E56.MirrorCS"),sQuery(id+"F1.wireOp",EDGE,"E23.MirrorCS"),sQuery(id+"F1.wireOp",EDGE,"E25.MirrorCS"),sQuery(id+"F1.wireOp",EDGE,"E39.MirrorCS"),sQuery(id+"F1.wireOp",EDGE,"E46.MirrorCS"),sQuery(id+"F1.wireOp",EDGE,"E37.MirrorCS"),sQuery(id+"F1.wireOp",EDGE,"E31.MirrorCS")])],"isStart":true})});
            var sketch = newSketch(context, id + "F6", { "sketchPlane" : qUnion([Q0])});
            skCircle(sketch, "E58", {"center": v(0, 0) * mm, "radius": 14.29 * mm});
            skSolve(sketch);
        }
        {
            var Q0;
            Q0=makeQuery(id+"F3.opChamfer","SPLIT",FACE,{"disambiguationData":[OD(0.0)],"derivedFrom":makeQuery(id+"F2.opExtrude","CAP_FACE",FACE,{"disambiguationData":[OSD([sQuery(id+"F1.wireOp",EDGE,"E6.2"),sQuery(id+"F1.wireOp",EDGE,"E6.3"),sQuery(id+"F1.wireOp",EDGE,"E6.4"),sQuery(id+"F1.wireOp",EDGE,"E6.5"),sQuery(id+"F1.wireOp",EDGE,"E6.7"),sQuery(id+"F1.wireOp",EDGE,"E5.3"),sQuery(id+"F1.wireOp",EDGE,"E5.10"),sQuery(id+"F1.wireOp",EDGE,"E5.11"),sQuery(id+"F1.wireOp",EDGE,"E9"),sQuery(id+"F1.wireOp",EDGE,"E10"),sQuery(id+"F1.wireOp",EDGE,"E13"),sQuery(id+"F1.wireOp",EDGE,"E14"),sQuery(id+"F1.wireOp",EDGE,"E15"),sQuery(id+"F1.wireOp",EDGE,"E18"),sQuery(id+"F1.wireOp",EDGE,"E19"),sQuery(id+"F1.wireOp",EDGE,"E20"),sQuery(id+"F1.wireOp",EDGE,"E26.MirrorCS"),sQuery(id+"F1.wireOp",EDGE,"E36.MirrorCS"),sQuery(id+"F1.wireOp",EDGE,"E38.MirrorCS"),sQuery(id+"F1.wireOp",EDGE,"E42.MirrorCS"),sQuery(id+"F1.wireOp",EDGE,"E43.MirrorCS"),sQuery(id+"F1.wireOp",EDGE,"E33.MirrorCS"),sQuery(id+"F1.wireOp",EDGE,"E47.MirrorCS"),sQuery(id+"F1.wireOp",EDGE,"E48.MirrorCS"),sQuery(id+"F1.wireOp",EDGE,"E49"),sQuery(id+"F1.wireOp",EDGE,"E50"),sQuery(id+"F1.wireOp",EDGE,"E51"),sQuery(id+"F1.wireOp",EDGE,"E52"),sQuery(id+"F1.wireOp",EDGE,"E53.MirrorCS"),sQuery(id+"F1.wireOp",EDGE,"E54.MirrorCS"),sQuery(id+"F1.wireOp",EDGE,"E55.MirrorCS"),sQuery(id+"F1.wireOp",EDGE,"E56.MirrorCS"),sQuery(id+"F1.wireOp",EDGE,"E23.MirrorCS"),sQuery(id+"F1.wireOp",EDGE,"E25.MirrorCS"),sQuery(id+"F1.wireOp",EDGE,"E39.MirrorCS"),sQuery(id+"F1.wireOp",EDGE,"E46.MirrorCS"),sQuery(id+"F1.wireOp",EDGE,"E37.MirrorCS"),sQuery(id+"F1.wireOp",EDGE,"E31.MirrorCS")])],"isStart":true})});
            var Q1;
            {var subQ5=sQuery(id+"F1.wireOp",EDGE,"E5.11");Q1=makeQuery(id+"F6.imprint","IMPRINT",FACE,{"disambiguationData":[TD([[makeQuery(id+"F6.imprint","IMPRINT",EDGE,{"derivedFrom":makeQuery(id+"F2.opExtrude","CAP_EDGE",EDGE,{"disambiguationData":[OSD([subQ5])],"isStart":true})}),-1.0]])]});}
            var Q2;
            {var subQ5=sQuery(id+"F1.wireOp",EDGE,"E6.7");Q2=makeQuery(id+"F6.imprint","IMPRINT",FACE,{"disambiguationData":[TD([[makeQuery(id+"F6.imprint","IMPRINT",EDGE,{"derivedFrom":makeQuery(id+"F2.opExtrude","CAP_EDGE",EDGE,{"disambiguationData":[OSD([subQ5])],"isStart":true})}),-1.0]])]});}
            var Q3;
            {var subQ5=sQuery(id+"F1.wireOp",EDGE,"E38.MirrorCS");Q3=makeQuery(id+"F6.imprint","IMPRINT",FACE,{"disambiguationData":[TD([[makeQuery(id+"F6.imprint","IMPRINT",EDGE,{"derivedFrom":makeQuery(id+"F2.opExtrude","CAP_EDGE",EDGE,{"disambiguationData":[OSD([subQ5])],"isStart":true})}),1.0]])]});}
            var Q4;
            {var subQ5=sQuery(id+"F1.wireOp",EDGE,"E26.MirrorCS");Q4=makeQuery(id+"F6.imprint","IMPRINT",FACE,{"disambiguationData":[TD([[makeQuery(id+"F6.imprint","IMPRINT",EDGE,{"derivedFrom":makeQuery(id+"F2.opExtrude","CAP_EDGE",EDGE,{"disambiguationData":[OSD([subQ5])],"isStart":true})}),1.0]])]});}
            var Q5;
            Q5=makeQuery(id+"F3.opChamfer","SPLIT",FACE,{"disambiguationData":[OD(1.0)],"derivedFrom":makeQuery(id+"F2.opExtrude","CAP_FACE",FACE,{"disambiguationData":[OSD([sQuery(id+"F1.wireOp",EDGE,"E6.2"),sQuery(id+"F1.wireOp",EDGE,"E6.3"),sQuery(id+"F1.wireOp",EDGE,"E6.4"),sQuery(id+"F1.wireOp",EDGE,"E6.5"),sQuery(id+"F1.wireOp",EDGE,"E6.7"),sQuery(id+"F1.wireOp",EDGE,"E5.3"),sQuery(id+"F1.wireOp",EDGE,"E5.10"),sQuery(id+"F1.wireOp",EDGE,"E5.11"),sQuery(id+"F1.wireOp",EDGE,"E9"),sQuery(id+"F1.wireOp",EDGE,"E10"),sQuery(id+"F1.wireOp",EDGE,"E13"),sQuery(id+"F1.wireOp",EDGE,"E14"),sQuery(id+"F1.wireOp",EDGE,"E15"),sQuery(id+"F1.wireOp",EDGE,"E18"),sQuery(id+"F1.wireOp",EDGE,"E19"),sQuery(id+"F1.wireOp",EDGE,"E20"),sQuery(id+"F1.wireOp",EDGE,"E26.MirrorCS"),sQuery(id+"F1.wireOp",EDGE,"E36.MirrorCS"),sQuery(id+"F1.wireOp",EDGE,"E38.MirrorCS"),sQuery(id+"F1.wireOp",EDGE,"E42.MirrorCS"),sQuery(id+"F1.wireOp",EDGE,"E43.MirrorCS"),sQuery(id+"F1.wireOp",EDGE,"E33.MirrorCS"),sQuery(id+"F1.wireOp",EDGE,"E47.MirrorCS"),sQuery(id+"F1.wireOp",EDGE,"E48.MirrorCS"),sQuery(id+"F1.wireOp",EDGE,"E49"),sQuery(id+"F1.wireOp",EDGE,"E50"),sQuery(id+"F1.wireOp",EDGE,"E51"),sQuery(id+"F1.wireOp",EDGE,"E52"),sQuery(id+"F1.wireOp",EDGE,"E53.MirrorCS"),sQuery(id+"F1.wireOp",EDGE,"E54.MirrorCS"),sQuery(id+"F1.wireOp",EDGE,"E55.MirrorCS"),sQuery(id+"F1.wireOp",EDGE,"E56.MirrorCS"),sQuery(id+"F1.wireOp",EDGE,"E23.MirrorCS"),sQuery(id+"F1.wireOp",EDGE,"E25.MirrorCS"),sQuery(id+"F1.wireOp",EDGE,"E39.MirrorCS"),sQuery(id+"F1.wireOp",EDGE,"E46.MirrorCS"),sQuery(id+"F1.wireOp",EDGE,"E37.MirrorCS"),sQuery(id+"F1.wireOp",EDGE,"E31.MirrorCS")])],"isStart":true})});
            extrude(context, id + "F7", {"entities" : qUnion([Q0, Q1, Q2, Q3, Q4, Q5]), "operationType" : NewBodyOperationType.REMOVE, "oppositeDirection" : true, "depth" : 1.78 * mm, "offsetDistance" : 25.4 * mm});
        }
    });
